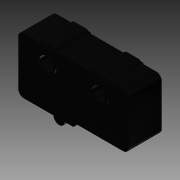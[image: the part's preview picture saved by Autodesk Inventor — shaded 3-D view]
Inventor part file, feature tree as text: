
AUTODESK INVENTOR PART (.ipt)
format: ipt  version: 2014 SP1 (Build 180222100, 222)  size: 184,320 bytes
history: native  units: mm
features: extrude x5, sketch x5, mirror x1, fillet x1
ambient origin geometry x8: Origin, YZ Plane, XZ Plane, XY Plane, X Axis, Y Axis, Z Axis, Center Point
bodies: Solid1 (feature_tree)
feature tree (12):
  extrude  "Extrusion1"  Depth=10.2mm
  extrude  "Extrusion2"  Depth=0.4mm
  extrude  "Extrusion4"  Depth=5.25mm
  mirror  "Mirror1"
  extrude  "Extrusion5"  Depth=6.0mm TaperAngle=0.0deg
  extrude  "Extrusion6"  Depth=1.0mm
  fillet  "Fillet1"  Radius=0.7mm
  sketch  "Sketch1"  dims[d0=20.0mm d1=10.2mm]
  sketch  "Sketch2"  dims[d2=0.4mm d3=0.5mm]
  sketch  "Sketch4"  dims[d4=2.4mm d5=5.25mm]
  sketch  "Sketch5"  dims[d6=9.5mm d7=6.0mm d8=0.0mm]
  sketch  "Sketch6"  dims[d9=10.5mm d10=0.5mm d11=0.7mm d12=6.0mm d13=0.0mm d18=3.4mm d19=0.2mm d20=0.0mm d21=2.5mm d22=2.4mm d23=0.2mm d24=0.0mm d25=6.4mm d26=2.0mm d27=1.0mm d28=4.0mm d29=0.0mm d30=1.0mm]
